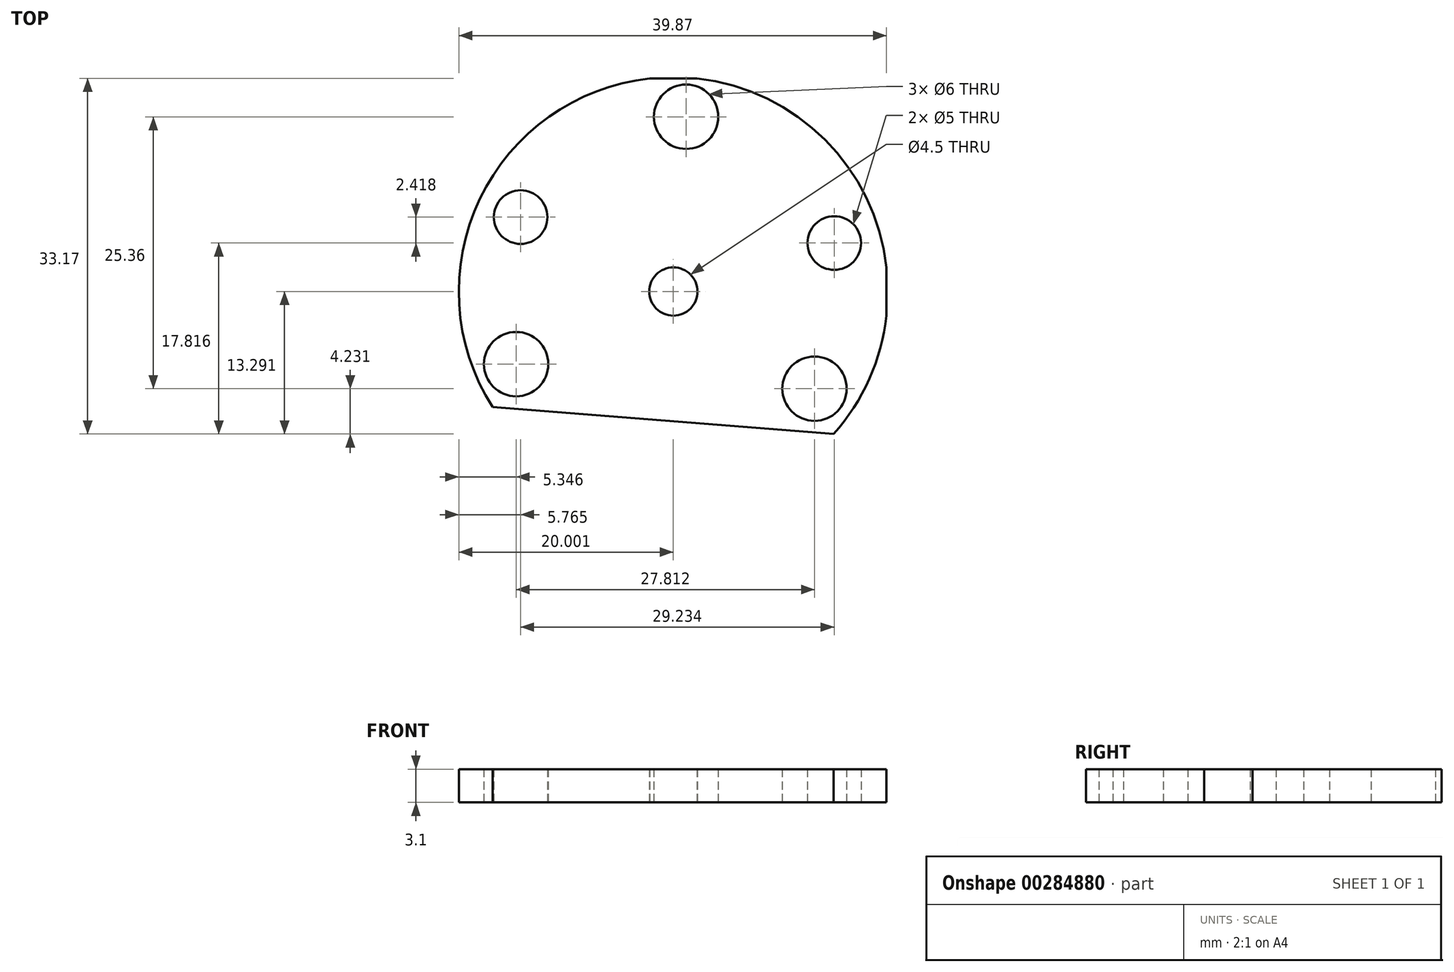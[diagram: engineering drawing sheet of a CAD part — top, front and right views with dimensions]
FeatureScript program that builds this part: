
annotation { "Feature Type Name" : "Feature", "Feature Type Description" : "" }
export const myFeature = defineFeature(function(context is Context, id is Id, definition is map)
    precondition{}
    {
        {
            var Q0;
            Q0=qCreatedBy(makeId("Top.planeOp"),FACE);
            var sketch = newSketch(context, id + "F0", { "sketchPlane" : qUnion([Q0])});
            skLineSegment(sketch, "E0.bottom", {"start": v(-5.92, -11.3) * mm, "end": v(34.08, -11.3) * mm});
            skLineSegment(sketch, "E0.top", {"start": v(-5.92, 28.7) * mm, "end": v(34.08, 28.7) * mm});
            skLineSegment(sketch, "E0.left", {"start": v(-5.92, -11.3) * mm, "end": v(-5.92, 28.7) * mm});
            skLineSegment(sketch, "E0.right", {"start": v(34.08, -11.3) * mm, "end": v(34.08, 28.7) * mm});
            skCircle(sketch, "E1", {"center": v(14.21, 8.82) * mm, "radius": 2.25 * mm});
            skCircle(sketch, "E2", {"center": v(29.2, 13.35) * mm, "radius": 2.5 * mm});
            skCircle(sketch, "E3", {"center": v(-0.03, 15.76) * mm, "radius": 2.5 * mm});
            skCircle(sketch, "E4", {"center": v(15.4, 25.12) * mm, "radius": 3 * mm});
            skCircle(sketch, "E5", {"center": v(27.37, -0.24) * mm, "radius": 3 * mm});
            skCircle(sketch, "E6", {"center": v(-0.44, 2.05) * mm, "radius": 3 * mm});
            skCircle(sketch, "E7", {"center": v(14.21, 8.82) * mm, "radius": 20 * mm});
            skLineSegment(sketch, "E8", {"start": v(29.16, -4.47) * mm, "end": v(-2.65, -1.94) * mm});
            skSolve(sketch);
        }
        {
            var Q0;
            Q0=makeQuery(id+"F0.imprint","IMPRINT",FACE,{"disambiguationData":[TD([[makeQuery(id+"F0.imprint","IMPRINT",EDGE,{"derivedFrom":sQuery(id+"F0.wireOp",EDGE,"E1")}),-1.0]])]});
            extrude(context, id + "F1", {"entities" : qUnion([Q0]), "depth" : 3.1 * mm});
        }
    });
